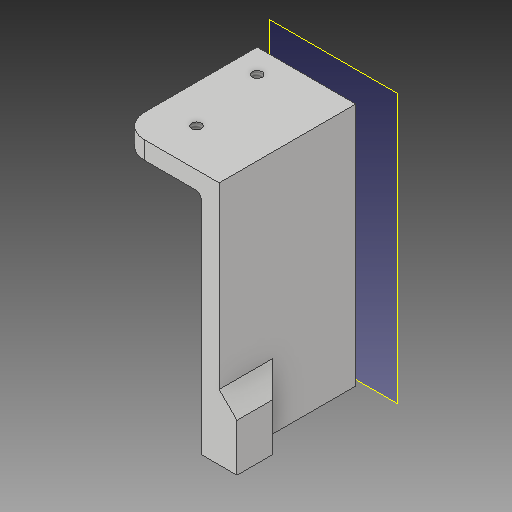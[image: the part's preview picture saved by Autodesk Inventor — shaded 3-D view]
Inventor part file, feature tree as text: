
AUTODESK INVENTOR PART (.ipt)
format: ipt  version: 2017 (Build 210142000, 142)  size: 210,432 bytes
history: native  units: in
note: dims shown in document units (in); Inventor stores cm internally (conversion verified against a paired STEP export)
features: sketch x6, projected_geometry x5, extrude x4, fillet x2, hole x2, chamfer x1, plane x1, mirror x1
ambient origin geometry x8: Origin, YZ Plane, XZ Plane, XY Plane, X Axis, Y Axis, Z Axis, Center Point
bodies: Solid1 (feature_tree)
feature tree (22):
  extrude  "Extrusion1"  Depth=0.636in
  extrude  "Extrusion3"  Depth=1.4375in
  extrude  "Extrusion4"  Depth=0.1875in TaperAngle=0.0deg
  fillet  "Fillet1"  Radius=1.25in
  extrude  "Extrusion5"  Depth=0.1875in TaperAngle=0.0deg
  chamfer  "Chamfer1"  Distance=0.375in
  hole  "Hole1"  [1 undecoded]
  hole  "Hole2"  [1 undecoded]
  fillet  "Fillet2"  Radius=0.5in
  plane  "Work Plane1"
  mirror  "Mirror1"
  sketch  "Sketch1"  dims[d0=2.57in d1=0.636in]
  sketch  "Sketch3"  dims[d4=0.1875in d5=0.0in d11=1.4375in]
  projected_geometry  "Projected Loop2"
  sketch  "Sketch4"  dims[d12=1.0375in d13=0.1875in d14=0.0in d15=1.25in]
  projected_geometry  "Projected Loop3"
  sketch  "Sketch6"  dims[d16=0.85in d17=0.1875in d18=0.0in]
  projected_geometry  "Projected Loop5"
  sketch  "Sketch8"  dims[d19=0.0625in]
  projected_geometry  "Projected Loop6"
  sketch  "Sketch9"  dims[d24=0.375in d25=0.375in d26=0.375in d27=0.375in d28=0.5in d29=0.0in d30=0.1875in d31=0.125in d32=45.0deg d33=0.104in d34=0.276in d35=0.375in d36=0.25in d37=0.5635in d38=0.5in d39=0.8108in d41=0.104in d42=0.276in d43=0.375in d44=0.25in d45=0.5635in d46=0.432in d47=0.8108in d50=1.25in d51=0.85in d52=0.25in d56=0.4in d57=0.25in d58=0.4in d59=0.25in]
  projected_geometry  "Projected Loop7"
note: 2 required parameter values undecoded (feature->parameter linkage not recoverable at this tier; creation-order binding heuristic only, values carry confidence <= 0.55)
